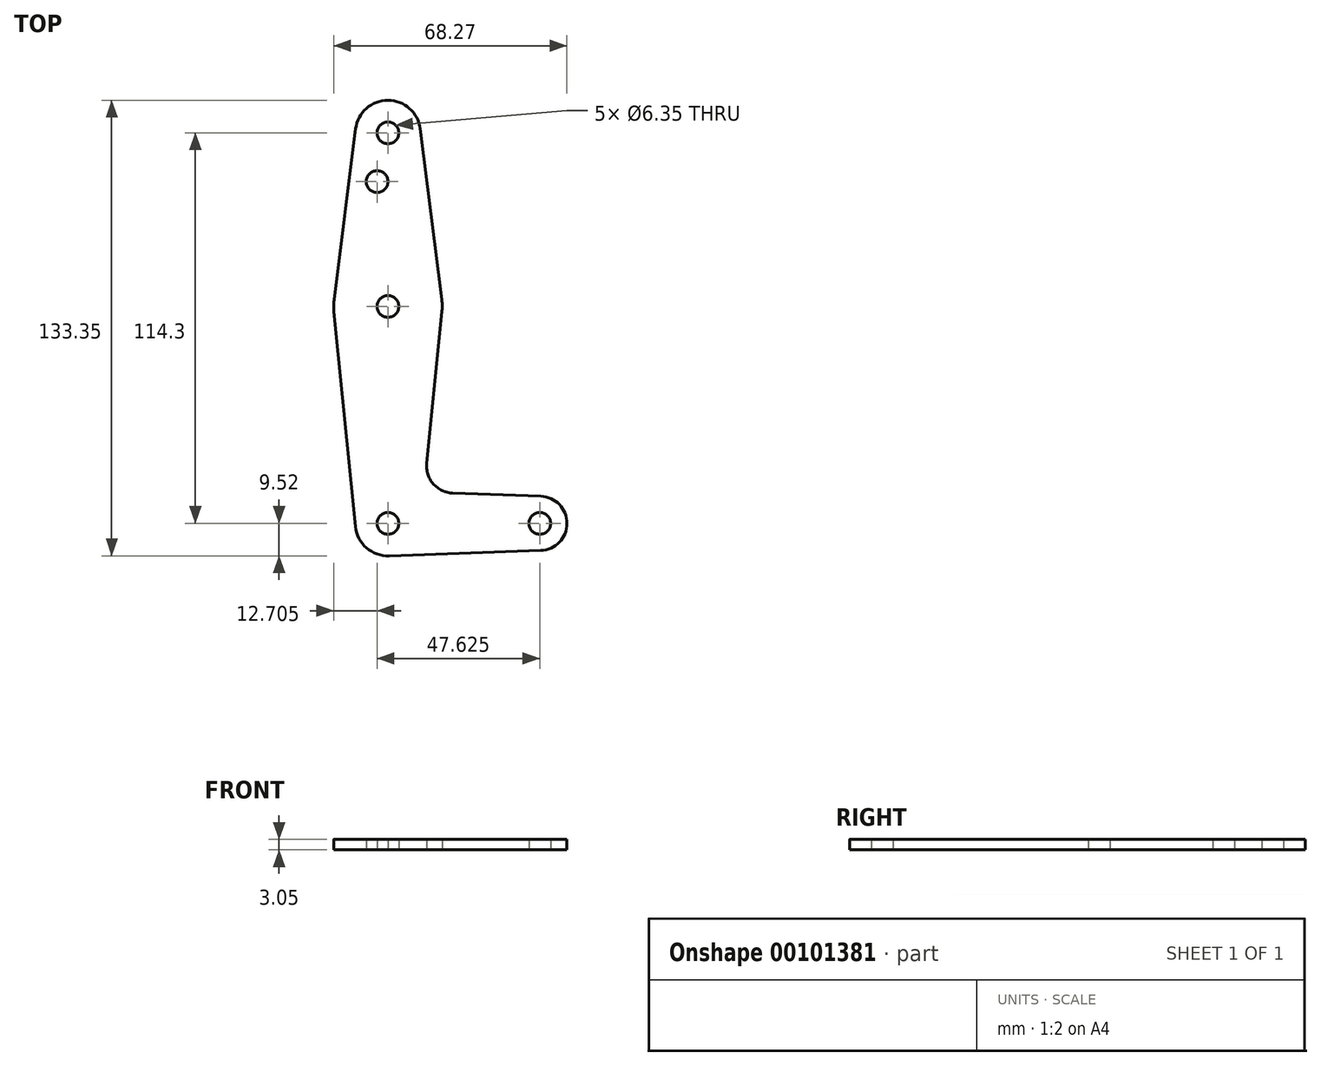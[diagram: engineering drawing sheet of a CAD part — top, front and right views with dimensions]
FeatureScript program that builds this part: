
annotation { "Feature Type Name" : "Feature", "Feature Type Description" : "" }
export const myFeature = defineFeature(function(context is Context, id is Id, definition is map)
    precondition{}
    {
        {
            var Q0;
            Q0=qCreatedBy(makeId("Top.planeOp"),FACE);
            var sketch = newSketch(context, id + "F0", { "sketchPlane" : qUnion([Q0])});
            skLineSegment(sketch, "E0", {"start": v(0, 0) * mm, "end": v(0, 114.3) * mm, "construction": true});
            skLineSegment(sketch, "E1", {"start": v(0, 0) * mm, "end": v(44.45, 0) * mm, "construction": true});
            skCircle(sketch, "E2", {"center": v(0, 114.3) * mm, "radius": 9.52 * mm});
            skCircle(sketch, "E3", {"center": v(0, 63.5) * mm, "radius": 15.88 * mm});
            skCircle(sketch, "E4", {"center": v(0, 0) * mm, "radius": 9.53 * mm});
            skCircle(sketch, "E5", {"center": v(44.45, 0) * mm, "radius": 7.94 * mm});
            skLineSegment(sketch, "E6", {"start": v(-9.45, 115.5) * mm, "end": v(-15.75, 65.48) * mm});
            skLineSegment(sketch, "E7", {"start": v(9.45, 115.5) * mm, "end": v(15.75, 65.48) * mm});
            skLineSegment(sketch, "E8", {"start": v(0.34, -9.52) * mm, "end": v(44.73, -7.93) * mm});
            skLineSegment(sketch, "E9", {"start": v(15.8, 61.91) * mm, "end": v(11.34, 17.6) * mm});
            skLineSegment(sketch, "E10", {"start": v(-15.8, 61.91) * mm, "end": v(-9.48, -0.95) * mm});
            skLineSegment(sketch, "E11", {"start": v(18.97, 8.85) * mm, "end": v(44.73, 7.93) * mm});
            skCircle(sketch, "E12", {"center": v(0, 114.3) * mm, "radius": 3.18 * mm});
            skCircle(sketch, "E13", {"center": v(0, 63.5) * mm, "radius": 3.18 * mm});
            skCircle(sketch, "E14", {"center": v(0, 0) * mm, "radius": 3.18 * mm});
            skCircle(sketch, "E15", {"center": v(44.45, 0) * mm, "radius": 3.18 * mm});
            skCircle(sketch, "E16", {"center": v(-3.18, 100.03) * mm, "radius": 3.18 * mm});
            skArc(sketch, "E17.filletArc", {"start": v(11.34, 17.6) * mm, "mid": v(13.26, 11.57) * mm, "end": v(18.97, 8.85) * mm});
            skSolve(sketch);
        }
        {
            var Q0;
            Q0=makeQuery(id+"F0.imprint","IMPRINT",FACE,{"disambiguationData":[TD([[makeQuery(id+"F0.imprint","IMPRINT",EDGE,{"derivedFrom":sQuery(id+"F0.wireOp",EDGE,"E12")}),-1.0]])]});
            var Q1;
            Q1=makeQuery(id+"F0.imprint","IMPRINT",FACE,{"disambiguationData":[TD([[makeQuery(id+"F0.imprint","IMPRINT",EDGE,{"derivedFrom":sQuery(id+"F0.wireOp",EDGE,"E14")}),-1.0]])]});
            var Q2;
            Q2=makeQuery(id+"F0.imprint","IMPRINT",FACE,{"disambiguationData":[TD([[makeQuery(id+"F0.imprint","IMPRINT",EDGE,{"derivedFrom":sQuery(id+"F0.wireOp",EDGE,"E15")}),-1.0]])]});
            var Q3;
            {var subQ1=sQuery(id+"F0.wireOp",EDGE,"E6");Q3=makeQuery(id+"F0.imprint","IMPRINT",FACE,{"disambiguationData":[TD([[makeQuery(id+"F0.imprint","IMPRINT",EDGE,{"derivedFrom":subQ1}),1.0]])]});}
            var Q4;
            Q4=makeQuery(id+"F0.imprint","IMPRINT",FACE,{"disambiguationData":[TD([[makeQuery(id+"F0.imprint","IMPRINT",EDGE,{"derivedFrom":sQuery(id+"F0.wireOp",EDGE,"E13")}),-1.0]])]});
            var Q5;
            {var subQ0=sQuery(id+"F0.wireOp",EDGE,"E8");Q5=makeQuery(id+"F0.imprint","IMPRINT",FACE,{"disambiguationData":[TD([[makeQuery(id+"F0.imprint","IMPRINT",EDGE,{"derivedFrom":subQ0}),1.0]])]});}
            extrude(context, id + "F1", {"entities" : qUnion([Q0, Q1, Q2, Q3, Q4, Q5]), "depth" : 3.05 * mm});
        }
    });
